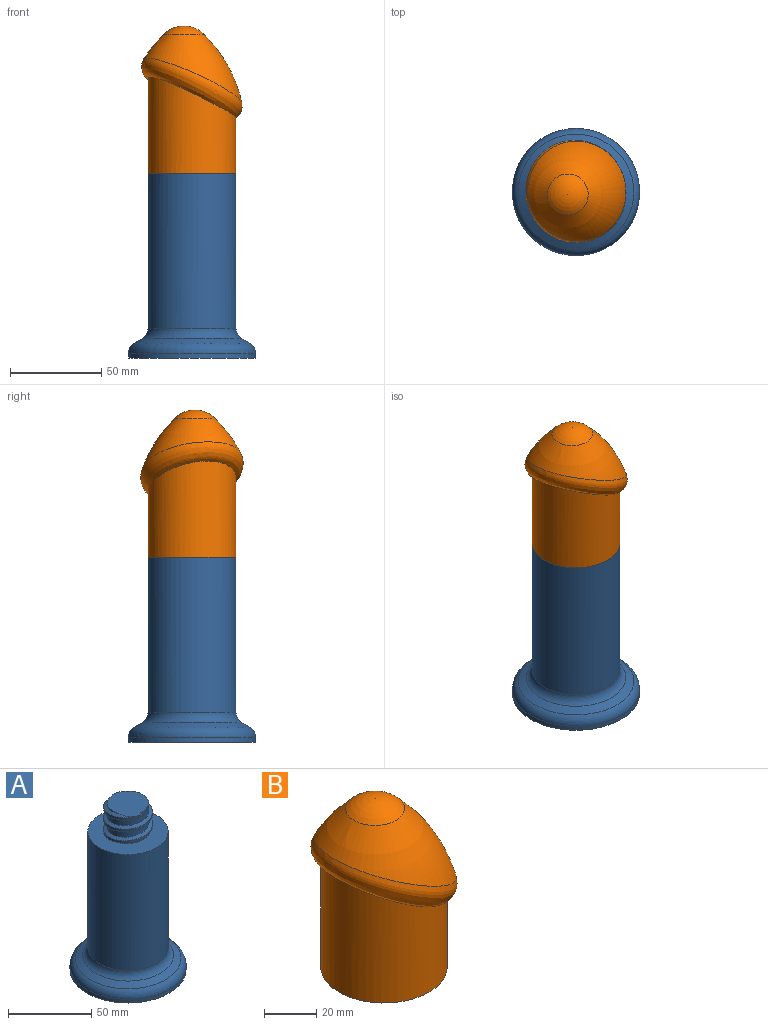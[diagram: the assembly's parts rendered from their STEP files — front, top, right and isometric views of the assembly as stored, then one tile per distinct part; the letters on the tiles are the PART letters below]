
ASSEMBLY  parts=2 mates=1
PART A: 15 faces, bbox 76.1x76.1x126.6 mm
  f0: cylinder r=14.73mm len=29.46mm, axis (0,0,-1), area 426.4mm2, adj f1,f2,f10,f11,f14
  f1: bspline ~29.46x29.46mm, area 524.1mm2, adj f0,f10,f11,f13
  f2: bspline ~29.46x29.46mm, area 479.9mm2, adj f0,f10,f13,f14
  f3: cylinder r=24.13mm len=85.35mm, axis (0,0,-1), area 12940.4mm2, adj f8,f10
  f4: plane 69.85x69.85mm, normal (0,0,-1), area 3832mm2, adj f5
  f5: cylinder r=34.92mm len=69.85mm, axis (0,0,1), area 588.9mm2, adj f4,f7
  f6: cone r=24.13mm half-angle=60deg, axis (0,0,-1), area 952.2mm2, adj f7,f8
  f7: torus R=28.57mm, axis (0,0,-1), area 1413.3mm2, adj f5,f6
  f8: torus R=30.48mm, axis (0,0,1), area 1054.1mm2, adj f3,f6
  f9: plane 2.57x0.07mm, normal (-0.4,0.92,0), area 0.1mm2, adj f10,f12,f13
  f10: plane 48.79x48.79mm, normal (0,0,1), area 1276.9mm2, adj f0,f1,f2,f3,f9,f13
  f11: plane 27.43x25.25mm, normal (0,0,1), area 510.6mm2, adj f0,f1,f13,f14
  f12: bspline ~10.42x5.93mm, area 0mm2, adj f9,f13
  f13: cylinder r=12.45mm len=24.89mm, axis (0,0,-1), area 927.9mm2, adj f1,f2,f9,f10,f11,f12,f14
  f14: plane 2.28x2.27mm, normal (0.99,-0.12,0), area 4.1mm2, adj f0,f2,f11,f13
PART B: 12 faces, bbox 64.6x64.6x82.3 mm
  f0: cylinder r=12.7mm len=25.4mm, axis (0,0,-1), area 1119.2mm2, adj f1,f2,f7,f8,f9,f11
  f1: bspline ~30.48x30.48mm, area 581.4mm2, adj f0,f8,f10,f11
  f2: plane 48.77x48.77mm, normal (0,0,-1), area 1203mm2, adj f0,f6,f9,f10,f11
  f3: sphere r=15.88mm, area 460.9mm2, adj f4
  f4: revolved ~64.08x64.08mm, area 3797.4mm2, adj f3,f5
  f5: bspline ~56.31x54.84mm, area 1980.3mm2, adj f4,f6
  f6: cylinder r=24.13mm len=52.73mm, axis (0,0,-1), area 6158.5mm2, adj f2,f5
  f7: plane 25.4x25.4mm, normal (0,0,-1), area 506.7mm2, adj f0
  f8: plane 4.06x2.54mm, normal (0,-1,0), area 7.7mm2, adj f0,f1,f9,f10
  f9: bspline ~30.48x30.48mm, area 711mm2, adj f0,f2,f8,f10
  f10: cylinder r=15.24mm len=30.48mm, axis (0,0,1), area 544.7mm2, adj f1,f2,f8,f9,f11
  f11: plane 2.07x2.05mm, normal (-0.59,0.81,0), area 3.9mm2, adj f0,f1,f2,f10
PLACE A at identity fixed
PLACE B rot(axis=(0,0,1),19.6deg) t=(0.28,-1.6,0)mm
MATE revolute A.f3 <-> B.f6  axis (0,0,1) through (4.78,0,-22.11)mm
